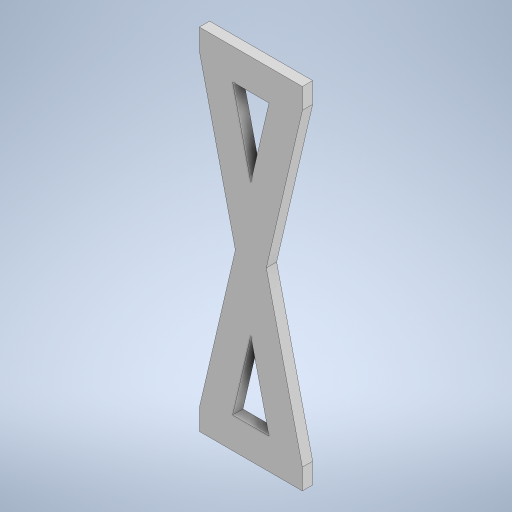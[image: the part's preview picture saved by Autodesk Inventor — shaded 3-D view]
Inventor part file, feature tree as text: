
AUTODESK INVENTOR PART (.ipt)
format: ipt  version: 2024 (Build 280153000, 153)  size: 306,176 bytes
history: native  units: in
note: dims shown in document units (in); Inventor stores cm internally (conversion verified against a paired STEP export)
features: extrude x2, sketch x1, pattern_linear x1, chamfer x1
ambient origin geometry x8: Origin, YZ Plane, XZ Plane, XY Plane, X Axis, Y Axis, Z Axis, Center Point
bodies: Solid1 (feature_tree)
feature tree (5):
  sketch  "Sketch1"  dims[d0=0.1614in d1=0.1614in d2=0.0807in d3=0.0807in d4=6.6929in d5=0.5906in d6=0.2953in d7=3.3465in d8=0.1969in d9=0.0in d10=0.1614in d11=0.0in d12=1.1811in d14=3.0457in d15=0.0197in d16=0.0787in d17=45.0deg d18=1.9685in d19=0.9843in d20=0.3937in d21=0.1969in d22=0.1969in]
  extrude  "Extrusion1"  Depth=0.1614in
  extrude  "Extrusion2"  Depth=0.1969in
  pattern_linear  "Rectangular Pattern1"  Spacing1=0.0807in  [1 undecoded]
  chamfer  "Chamfer1"  Distance=6.6929in
note: 1 required parameter value undecoded (feature->parameter linkage not recoverable at this tier; creation-order binding heuristic only, values carry confidence <= 0.55)
